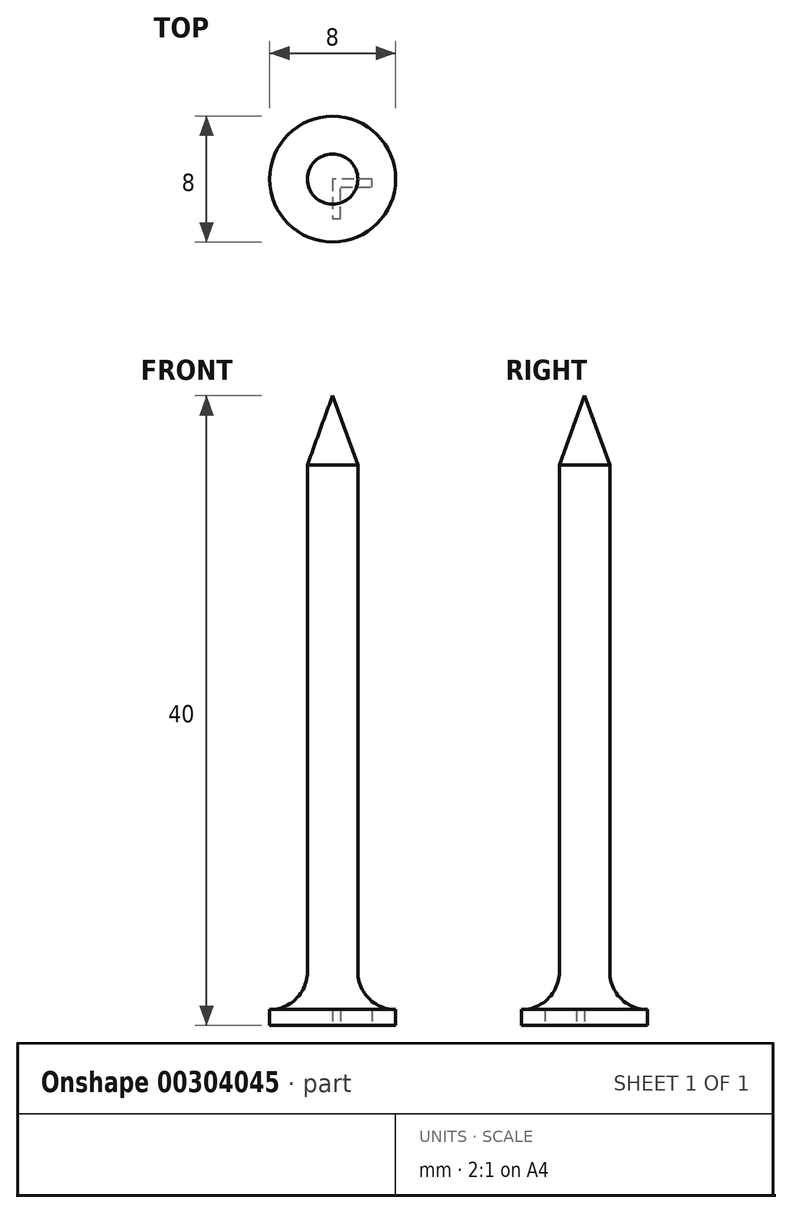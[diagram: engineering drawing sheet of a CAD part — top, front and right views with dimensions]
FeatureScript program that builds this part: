
annotation { "Feature Type Name" : "Feature", "Feature Type Description" : "" }
export const myFeature = defineFeature(function(context is Context, id is Id, definition is map)
    precondition{}
    {
        {
            var Q0;
            Q0=qCreatedBy(makeId("Front.planeOp"),FACE);
            var sketch = newSketch(context, id + "F0", { "sketchPlane" : qUnion([Q0])});
            skLineSegment(sketch, "E0", {"start": v(0, 0) * mm, "end": v(0, 40) * mm, "construction": true});
            skLineSegment(sketch, "E1", {"start": v(0, 40) * mm, "end": v(1.6, 35.6) * mm});
            skLineSegment(sketch, "E2", {"start": v(1.6, 35.6) * mm, "end": v(1.6, 3.4) * mm});
            skLineSegment(sketch, "E3", {"start": v(0, 0) * mm, "end": v(4, 0) * mm});
            skLineSegment(sketch, "E4", {"start": v(4, 0) * mm, "end": v(4, 1) * mm});
            skArc(sketch, "E5", {"start": v(1.6, 3.4) * mm, "mid": v(2.3, 1.7) * mm, "end": v(4, 1) * mm});
            skLineSegment(sketch, "E6", {"start": v(0, 40) * mm, "end": v(0, 0) * mm});
            skSolve(sketch);
        }
        {
            var Q0;
            Q0 = qSketchRegion(id + "F0", true);
            var Q1;
            Q1=sQuery(id+"F0.wireOp",EDGE,"E0");
            revolve(context, id + "F1", {"entities" : qUnion([Q0]), "axis" : qUnion([Q1]), "revolveType" : RevolveType.FULL});
        }
        {
            var Q0;
            Q0=qCreatedBy(makeId("Top.planeOp"),FACE);
            var sketch = newSketch(context, id + "F2", { "sketchPlane" : qUnion([Q0])});
            skLineSegment(sketch, "E7", {"start": v(0, 0) * mm, "end": v(0, -2.5) * mm});
            skLineSegment(sketch, "E8", {"start": v(0, -2.5) * mm, "end": v(0.5, -2.5) * mm});
            skLineSegment(sketch, "E9", {"start": v(0.5, -2.5) * mm, "end": v(0.5, -0.5) * mm});
            skLineSegment(sketch, "E10", {"start": v(0.5, -0.5) * mm, "end": v(2.5, -0.5) * mm});
            skLineSegment(sketch, "E11", {"start": v(2.5, -0.5) * mm, "end": v(2.5, 0) * mm});
            skLineSegment(sketch, "E12", {"start": v(2.5, 0) * mm, "end": v(0, 0) * mm});
            skSolve(sketch);
        }
        {
            var Q0;
            Q0 = qSketchRegion(id + "F2", true);
            extrude(context, id + "F3", {"entities" : qUnion([Q0]), "operationType" : NewBodyOperationType.REMOVE, "depth" : 1 * mm});
        }
    });
